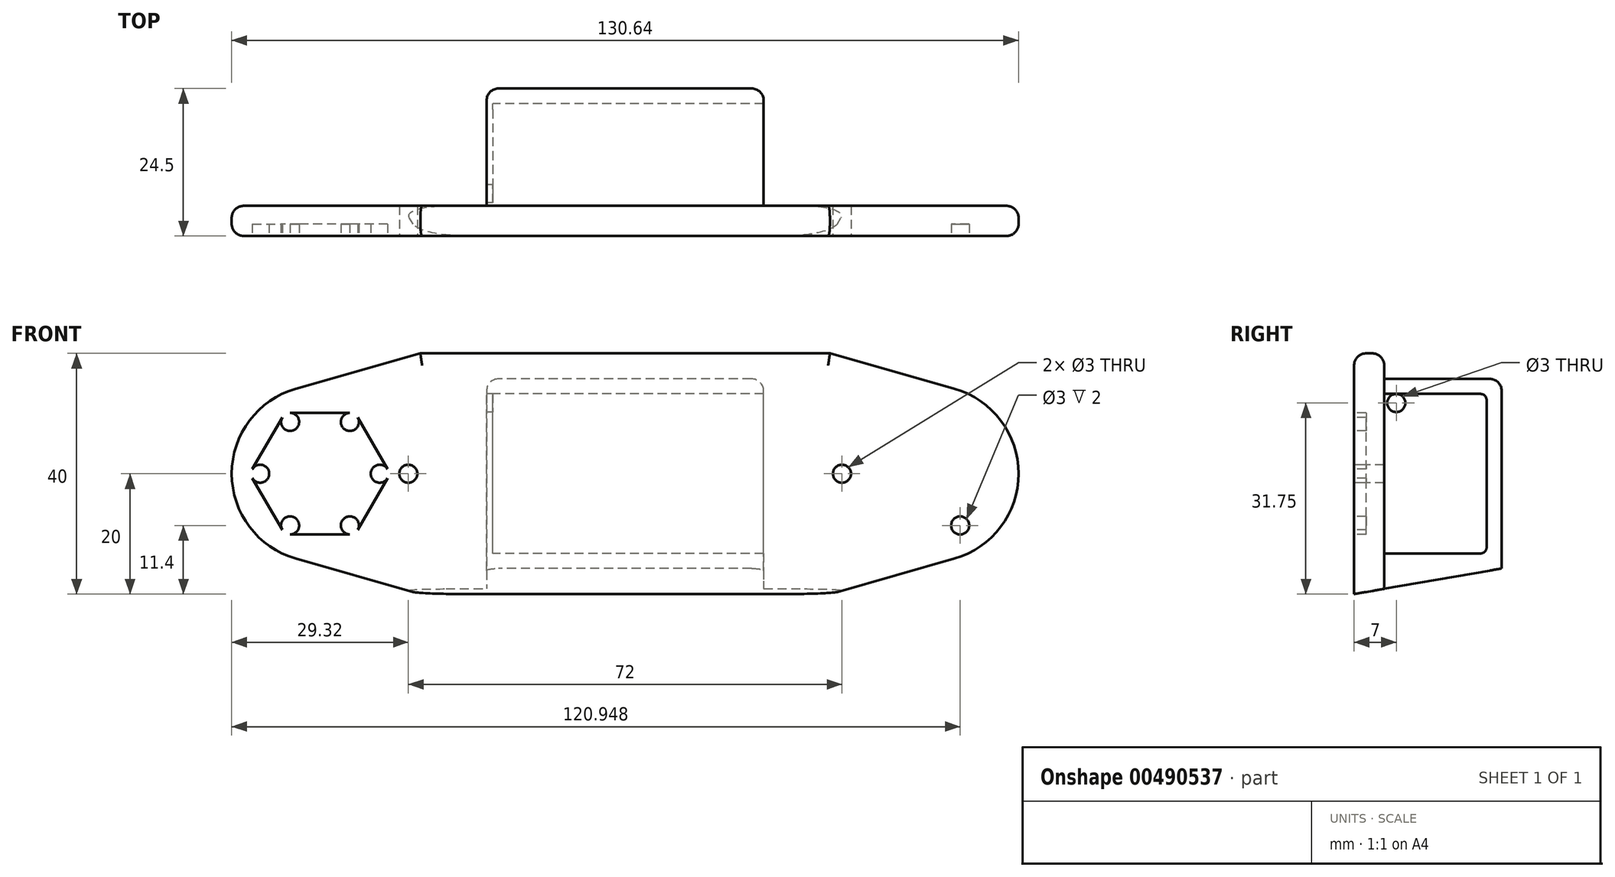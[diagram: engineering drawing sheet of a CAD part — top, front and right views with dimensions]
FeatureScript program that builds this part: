
annotation { "Feature Type Name" : "Feature", "Feature Type Description" : "" }
export const myFeature = defineFeature(function(context is Context, id is Id, definition is map)
    precondition{}
    {
        {
            var Q0;
            Q0=qCreatedBy(makeId("Front.planeOp"),FACE);
            var sketch = newSketch(context, id + "F0", { "sketchPlane" : qUnion([Q0])});
            skLineSegment(sketch, "E0.bottom", {"start": v(34, 30) * mm, "end": v(-34, 30) * mm});
            skLineSegment(sketch, "E0.top", {"start": v(34, -30) * mm, "end": v(-34, -30) * mm});
            skLineSegment(sketch, "E0.left", {"start": v(34, 30) * mm, "end": v(34, -30) * mm});
            skLineSegment(sketch, "E0.right", {"start": v(-34, 30) * mm, "end": v(-34, -30) * mm});
            skPoint(sketch, "E0.middle", {"position": v(0, 0) * mm});
            skSolve(sketch);
        }
        {
            var Q0;
            Q0=qCreatedBy(makeId("Front.planeOp"),FACE);
            var sketch = newSketch(context, id + "F1", { "sketchPlane" : qUnion([Q0])});
            skCircle(sketch, "E1.cCircle", {"center": v(-50.66, 0) * mm, "radius": 10.1 * mm, "construction": true});
            skLineSegment(sketch, "E1.0", {"start": v(-44.83, -10.1) * mm, "end": v(-56.5, -10.1) * mm});
            skLineSegment(sketch, "E1.1", {"start": v(-56.5, -10.1) * mm, "end": v(-62.32, 0) * mm});
            skLineSegment(sketch, "E1.2", {"start": v(-62.32, 0) * mm, "end": v(-56.5, 10.1) * mm});
            skLineSegment(sketch, "E1.3", {"start": v(-56.5, 10.1) * mm, "end": v(-44.83, 10.1) * mm});
            skLineSegment(sketch, "E1.4", {"start": v(-44.83, 10.1) * mm, "end": v(-39, 0) * mm});
            skLineSegment(sketch, "E1.5", {"start": v(-39, 0) * mm, "end": v(-44.83, -10.1) * mm});
            skPoint(sketch, "E1.0.midPoint", {"position": v(-50.66, -10.1) * mm});
            skCircle(sketch, "E2", {"center": v(-55.63, -8.6) * mm, "radius": 1.5 * mm});
            skCircle(sketch, "E3.1.0", {"center": v(-45.7, -8.6) * mm, "radius": 1.5 * mm});
            skCircle(sketch, "E3.2.0", {"center": v(-40.73, 0) * mm, "radius": 1.5 * mm});
            skCircle(sketch, "E3.3.0", {"center": v(-45.7, 8.6) * mm, "radius": 1.5 * mm});
            skCircle(sketch, "E3.4.0", {"center": v(-55.63, 8.6) * mm, "radius": 1.5 * mm});
            skCircle(sketch, "E3.5.0", {"center": v(-60.6, 0) * mm, "radius": 1.5 * mm});
            skCircle(sketch, "E4.MirrorC", {"center": v(55.63, -8.6) * mm, "radius": 1.5 * mm});
            skCircle(sketch, "E5.MirrorC", {"center": v(55.63, 8.6) * mm, "radius": 1.5 * mm});
            skCircle(sketch, "E6.MirrorC", {"center": v(45.7, -8.6) * mm, "radius": 1.5 * mm});
            skCircle(sketch, "E7.MirrorC", {"center": v(40.73, 0) * mm, "radius": 1.5 * mm});
            skCircle(sketch, "E8.MirrorC", {"center": v(50.66, 0) * mm, "radius": 10.1 * mm, "construction": true});
            skLineSegment(sketch, "E9.MirrorCS", {"start": v(44.83, -10.1) * mm, "end": v(56.5, -10.1) * mm});
            skLineSegment(sketch, "E10.MirrorCS", {"start": v(44.83, 10.1) * mm, "end": v(39, 0) * mm});
            skCircle(sketch, "E11.MirrorC", {"center": v(45.7, 8.6) * mm, "radius": 1.5 * mm});
            skLineSegment(sketch, "E12.MirrorCS", {"start": v(56.5, -10.1) * mm, "end": v(62.32, 0) * mm});
            skLineSegment(sketch, "E13.MirrorCS", {"start": v(39, 0) * mm, "end": v(44.83, -10.1) * mm});
            skPoint(sketch, "E14.MirrorP", {"position": v(50.66, -10.1) * mm});
            skLineSegment(sketch, "E15.MirrorCS", {"start": v(56.5, 10.1) * mm, "end": v(44.83, 10.1) * mm});
            skCircle(sketch, "E16.MirrorC", {"center": v(60.6, 0) * mm, "radius": 1.5 * mm});
            skLineSegment(sketch, "E17.MirrorCS", {"start": v(62.32, 0) * mm, "end": v(56.5, 10.1) * mm});
            skPoint(sketch, "E18", {"position": v(36, 0) * mm});
            skPoint(sketch, "E19.MirrorP", {"position": v(-36, 0) * mm});
            skSolve(sketch);
        }
        {
            var Q0;
            Q0=qCreatedBy(makeId("Front.planeOp"),FACE);
            var sketch = newSketch(context, id + "F2", { "sketchPlane" : qUnion([Q0])});
            skLineSegment(sketch, "E20.0.0", {"start": v(-34, -30) * mm, "end": v(34, -30) * mm, "construction": true});
            skLineSegment(sketch, "E20.0.1", {"start": v(34, -30) * mm, "end": v(34, 30) * mm, "construction": true});
            skLineSegment(sketch, "E20.0.2", {"start": v(34, 30) * mm, "end": v(-34, 30) * mm, "construction": true});
            skLineSegment(sketch, "E20.0.3", {"start": v(-34, 30) * mm, "end": v(-34, -30) * mm, "construction": true});
            skLineSegment(sketch, "E21.0.0", {"start": v(-39.43, 0.75) * mm, "end": v(-44.4, 9.35) * mm, "construction": true});
            skArc(sketch, "E21.0.1", {"start": v(-44.4, 9.35) * mm, "mid": v(-46.45, 7.3) * mm, "end": v(-45.7, 10.1) * mm, "construction": true});
            skLineSegment(sketch, "E21.0.2", {"start": v(-45.7, 10.1) * mm, "end": v(-55.63, 10.1) * mm, "construction": true});
            skArc(sketch, "E21.0.3", {"start": v(-55.63, 10.1) * mm, "mid": v(-54.88, 7.3) * mm, "end": v(-56.93, 9.35) * mm, "construction": true});
            skLineSegment(sketch, "E21.0.4", {"start": v(-56.93, 9.35) * mm, "end": v(-61.9, 0.75) * mm, "construction": true});
            skArc(sketch, "E21.0.5", {"start": v(-61.9, 0.75) * mm, "mid": v(-59.1, 0) * mm, "end": v(-61.9, -0.75) * mm, "construction": true});
            skLineSegment(sketch, "E21.0.6", {"start": v(-61.9, -0.75) * mm, "end": v(-56.93, -9.35) * mm, "construction": true});
            skArc(sketch, "E21.0.7", {"start": v(-56.93, -9.35) * mm, "mid": v(-54.88, -7.3) * mm, "end": v(-55.63, -10.1) * mm, "construction": true});
            skLineSegment(sketch, "E21.0.8", {"start": v(-55.63, -10.1) * mm, "end": v(-45.7, -10.1) * mm, "construction": true});
            skArc(sketch, "E21.0.9", {"start": v(-45.7, -10.1) * mm, "mid": v(-46.45, -7.3) * mm, "end": v(-44.4, -9.35) * mm, "construction": true});
            skLineSegment(sketch, "E21.0.10", {"start": v(-44.4, -9.35) * mm, "end": v(-39.43, -0.75) * mm, "construction": true});
            skArc(sketch, "E21.0.11", {"start": v(-39.43, -0.75) * mm, "mid": v(-42.23, 0) * mm, "end": v(-39.43, 0.75) * mm, "construction": true});
            skArc(sketch, "E22.0.0", {"start": v(45.7, 10.1) * mm, "mid": v(46.45, 7.3) * mm, "end": v(44.4, 9.35) * mm, "construction": true});
            skLineSegment(sketch, "E22.0.1", {"start": v(44.4, 9.35) * mm, "end": v(39.43, 0.75) * mm, "construction": true});
            skArc(sketch, "E22.0.2", {"start": v(39.43, 0.75) * mm, "mid": v(42.23, 0) * mm, "end": v(39.43, -0.75) * mm, "construction": true});
            skLineSegment(sketch, "E22.0.3", {"start": v(39.43, -0.75) * mm, "end": v(44.4, -9.35) * mm, "construction": true});
            skArc(sketch, "E22.0.4", {"start": v(44.4, -9.35) * mm, "mid": v(46.45, -7.3) * mm, "end": v(45.7, -10.1) * mm, "construction": true});
            skLineSegment(sketch, "E22.0.5", {"start": v(45.7, -10.1) * mm, "end": v(55.63, -10.1) * mm, "construction": true});
            skArc(sketch, "E22.0.6", {"start": v(55.63, -10.1) * mm, "mid": v(54.88, -7.3) * mm, "end": v(56.93, -9.35) * mm, "construction": true});
            skLineSegment(sketch, "E22.0.7", {"start": v(56.93, -9.35) * mm, "end": v(61.9, -0.75) * mm, "construction": true});
            skArc(sketch, "E22.0.8", {"start": v(61.9, -0.75) * mm, "mid": v(59.1, 0) * mm, "end": v(61.9, 0.75) * mm, "construction": true});
            skLineSegment(sketch, "E22.0.9", {"start": v(61.9, 0.75) * mm, "end": v(56.93, 9.35) * mm, "construction": true});
            skArc(sketch, "E22.0.10", {"start": v(56.93, 9.35) * mm, "mid": v(54.88, 7.3) * mm, "end": v(55.63, 10.1) * mm, "construction": true});
            skLineSegment(sketch, "E22.0.11", {"start": v(55.63, 10.1) * mm, "end": v(45.7, 10.1) * mm, "construction": true});
            skArc(sketch, "E23", {"start": v(-54.68, 14.1) * mm, "mid": v(-65.32, 0) * mm, "end": v(-54.68, -14.1) * mm});
            skPoint(sketch, "E23.centerSnap0", {"position": v(-50.66, 10.1) * mm});
            skPoint(sketch, "E24.0", {"position": v(50.66, 0) * mm});
            skArc(sketch, "E25", {"start": v(54.68, -14.1) * mm, "mid": v(65.32, 0) * mm, "end": v(54.68, 14.1) * mm});
            skLineSegment(sketch, "E26", {"start": v(-54.68, 14.1) * mm, "end": v(-34, 20) * mm});
            skLineSegment(sketch, "E27", {"start": v(-54.68, -14.1) * mm, "end": v(-34, -20) * mm});
            skLineSegment(sketch, "E28", {"start": v(-34, 20) * mm, "end": v(34, 20) * mm});
            skLineSegment(sketch, "E29", {"start": v(-34, -20) * mm, "end": v(34, -20) * mm});
            skLineSegment(sketch, "E30.MirrorCS", {"start": v(54.68, 14.1) * mm, "end": v(34, 20) * mm});
            skLineSegment(sketch, "E31.MirrorCS", {"start": v(54.68, -14.1) * mm, "end": v(34, -20) * mm});
            skSolve(sketch);
        }
        {
            var Q0;
            Q0=makeQuery(id+"F2.imprint","IMPRINT",FACE,{"disambiguationData":[TD([[makeQuery(id+"F2.imprint","IMPRINT",EDGE,{"derivedFrom":sQuery(id+"F2.wireOp",EDGE,"E23")}),1.0]])]});
            extrude(context, id + "F3", {"entities" : qUnion([Q0]), "oppositeDirection" : true, "depth" : 5 * mm});
        }
        {
            var Q0;
            {var subQ6=sQuery(id+"F1.wireOp",EDGE,"E1.0");var subQ13=sQuery(id+"F1.wireOp",EDGE,"E3.1.0");var subQ16=makeQuery(id+"F1.imprint","INTERSECT",VERTEX,{"derivedFrom":[subQ6,subQ13]});Q0=makeQuery(id+"F1.imprint","IMPRINT",FACE,{"disambiguationData":[TD([[makeQuery(id+"F1.imprint","IMPRINT",EDGE,{"disambiguationData":[TD([[subQ16,-1.0]])],"derivedFrom":subQ6}),-1.0]])]});}
            var Q1;
            {var subQ1=sQuery(id+"F1.wireOp",EDGE,"E4.MirrorC");var subQ15=sQuery(id+"F1.wireOp",EDGE,"E9.MirrorCS");var subQ16=makeQuery(id+"F1.imprint","INTERSECT",VERTEX,{"derivedFrom":[subQ1,subQ15]});Q1=makeQuery(id+"F1.imprint","IMPRINT",FACE,{"disambiguationData":[TD([[makeQuery(id+"F1.imprint","IMPRINT",EDGE,{"disambiguationData":[TD([[subQ16,-1.0]])],"derivedFrom":subQ1}),1.0]])]});}
            extrude(context, id + "F4", {"entities" : qUnion([Q0, Q1]), "operationType" : NewBodyOperationType.REMOVE, "oppositeDirection" : true, "depth" : 2 * mm});
        }
        {
            var Q0;
            Q0=qCreatedBy(makeId("Right.planeOp"),FACE);
            var sketch = newSketch(context, id + "F5", { "sketchPlane" : qUnion([Q0])});
            skLineSegment(sketch, "E32.0", {"start": v(5, -14.1) * mm, "end": v(5, 14.1) * mm, "construction": true});
            skLineSegment(sketch, "E33.bottom", {"start": v(22, -13.25) * mm, "end": v(5, -13.25) * mm});
            skLineSegment(sketch, "E33.top", {"start": v(22, 13.25) * mm, "end": v(5, 13.25) * mm});
            skLineSegment(sketch, "E33.left", {"start": v(22, -13.25) * mm, "end": v(22, 13.25) * mm});
            skLineSegment(sketch, "E33.right", {"start": v(5, -13.25) * mm, "end": v(5, 13.25) * mm});
            skPoint(sketch, "E33.middle", {"position": v(13.5, 0) * mm});
            skLineSegment(sketch, "E34.0", {"start": v(24.5, 15.75) * mm, "end": v(5, 15.75) * mm});
            skLineSegment(sketch, "E34.1", {"start": v(24.5, -15.75) * mm, "end": v(24.5, 15.75) * mm});
            skLineSegment(sketch, "E35", {"start": v(5, 13.25) * mm, "end": v(5, 15.75) * mm});
            skLineSegment(sketch, "E36", {"start": v(24.5, -15.75) * mm, "end": v(0, -20) * mm});
            skPoint(sketch, "E37.0", {"position": v(0, -20) * mm});
            skLineSegment(sketch, "E38", {"start": v(5, -13.25) * mm, "end": v(5, -19.13) * mm});
            skPoint(sketch, "E39.0", {"position": v(5, -20) * mm});
            skLineSegment(sketch, "E40", {"start": v(5, -19.13) * mm, "end": v(5, -20) * mm});
            skLineSegment(sketch, "E41", {"start": v(0, -20) * mm, "end": v(5, -20) * mm});
            skSolve(sketch);
        }
        {
            var Q0;
            Q0=makeQuery(id+"F5.imprint","IMPRINT",FACE,{"disambiguationData":[TD([[makeQuery(id+"F5.imprint","IMPRINT",EDGE,{"derivedFrom":sQuery(id+"F5.wireOp",EDGE,"E33.bottom")}),1.0]])]});
            extrude(context, id + "F6", {"entities" : qUnion([Q0]), "operationType" : NewBodyOperationType.ADD, "endBound" : BoundingType.SYMMETRIC, "depth" : 46 * mm});
        }
        {
            var Q0;
            Q0=makeQuery(id+"F5.imprint","IMPRINT",FACE,{"disambiguationData":[TD([[makeQuery(id+"F5.imprint","IMPRINT",EDGE,{"derivedFrom":sQuery(id+"F5.wireOp",EDGE,"E33.bottom")}),-1.0]])]});
            var Q1;
            Q1=makeQuery(id+"F6.opExtrude","CAP_FACE",FACE,{"disambiguationData":[OSD([sQuery(id+"F5.wireOp",EDGE,"E33.bottom"),sQuery(id+"F5.wireOp",EDGE,"E33.top"),sQuery(id+"F5.wireOp",EDGE,"E33.left"),sQuery(id+"F5.wireOp",EDGE,"E34.0"),sQuery(id+"F5.wireOp",EDGE,"E34.1"),sQuery(id+"F5.wireOp",EDGE,"E35"),sQuery(id+"F5.wireOp",EDGE,"E36"),sQuery(id+"F5.wireOp",EDGE,"oWYAaW46-Xd7K-HqAU-Cgo2-wgBWHUBuq2t6")])],"isStart":true});
            extrude(context, id + "F7", {"entities" : qUnion([Q0]), "operationType" : NewBodyOperationType.ADD, "endBound" : BoundingType.UP_TO_SURFACE, "oppositeDirection" : true, "endBoundEntityFace" : qUnion([Q1]), "depth" : 25 * mm, "hasSecondDirection" : true, "secondDirectionOppositeDirection" : true, "secondDirectionDepth" : 22 * mm});
        }
        {
            var Q0;
            Q0=sQuery(id+"F1.wireOp",VERTEX,"E19.MirrorP");
            var Q1;
            Q1=sQuery(id+"F1.wireOp",VERTEX,"E18");
            var Q2;
            Q2=makeQuery(id+"F3.opExtrude","SWEPT_BODY",BODY,{"disambiguationData":[OSD([sQuery(id+"F2.wireOp",EDGE,"E23"),sQuery(id+"F2.wireOp",EDGE,"E25"),sQuery(id+"F2.wireOp",EDGE,"E26"),sQuery(id+"F2.wireOp",EDGE,"E27"),sQuery(id+"F2.wireOp",EDGE,"E28"),sQuery(id+"F2.wireOp",EDGE,"E29"),sQuery(id+"F2.wireOp",EDGE,"E30.MirrorCS"),sQuery(id+"F2.wireOp",EDGE,"E31.MirrorCS")])]});
            hole(context, id + "F8", {"style" : HoleStyle.SIMPLE, "endStyle" : HoleEndStyle.THROUGH, "holeDiameter" : 3 * mm, "isTappedThrough" : true, "tappedDepth" : 12 * mm, "tapClearance" : 3, "locations" : qUnion([Q0, Q1]), "scope" : qUnion([Q2])});
        }
        {
            var Q0;
            {var subQ0=sQuery(id+"F5.wireOp",EDGE,"E38");var subQ1=sQuery(id+"F5.wireOp",EDGE,"E36");var subQ2=sQuery(id+"F5.wireOp",EDGE,"E35");var subQ3=sQuery(id+"F5.wireOp",EDGE,"E34.1");var subQ4=sQuery(id+"F5.wireOp",EDGE,"E34.0");var subQ5=sQuery(id+"F5.wireOp",EDGE,"E33.left");var subQ6=sQuery(id+"F5.wireOp",EDGE,"E33.top");var subQ7=sQuery(id+"F5.wireOp",EDGE,"E33.bottom");Q0=makeQuery(id+"F7.boolean.opBoolean","MERGE",FACE,{"derivedFrom":[makeQuery(id+"F6.opExtrude","CAP_FACE",FACE,{"disambiguationData":[OSD([subQ7,subQ6,subQ5,subQ4,subQ3,subQ2,subQ1,subQ0])],"isStart":true}),makeQuery(id+"F7.opExtrude","CAP_FACE",FACE,{"disambiguationData":[OSD([subQ7,subQ6,subQ5,subQ4,subQ3,subQ2,subQ1,subQ0])],"isStart":false})]});}
            var sketch = newSketch(context, id + "F9", { "sketchPlane" : qUnion([Q0])});
            skPoint(sketch, "E42", {"position": v(-7, 11.75) * mm});
            skSolve(sketch);
        }
        {
            var Q0;
            Q0=sQuery(id+"F9.wireOp",VERTEX,"E42");
            var Q1;
            Q1=makeQuery(id+"F3.opExtrude","SWEPT_BODY",BODY,{"disambiguationData":[OSD([sQuery(id+"F2.wireOp",EDGE,"E23"),sQuery(id+"F2.wireOp",EDGE,"E25"),sQuery(id+"F2.wireOp",EDGE,"E26"),sQuery(id+"F2.wireOp",EDGE,"E27"),sQuery(id+"F2.wireOp",EDGE,"E28"),sQuery(id+"F2.wireOp",EDGE,"E29"),sQuery(id+"F2.wireOp",EDGE,"E30.MirrorCS"),sQuery(id+"F2.wireOp",EDGE,"E31.MirrorCS")])]});
            hole(context, id + "F10", {"style" : HoleStyle.SIMPLE, "endStyle" : HoleEndStyle.THROUGH, "holeDiameter" : 3 * mm, "isTappedThrough" : true, "tappedDepth" : 12 * mm, "tapClearance" : 3, "locations" : qUnion([Q0]), "scope" : qUnion([Q1])});
        }
        {
            var Q0;
            {var subQ2=sQuery(id+"F5.wireOp",EDGE,"E40");Q0=makeQuery(id+"F5.imprint","IMPRINT",FACE,{"disambiguationData":[TD([[makeQuery(id+"F5.imprint","IMPRINT",EDGE,{"derivedFrom":subQ2}),-1.0]])]});}
            extrude(context, id + "F11", {"entities" : qUnion([Q0]), "operationType" : NewBodyOperationType.REMOVE, "endBound" : BoundingType.SYMMETRIC, "oppositeDirection" : true, "depth" : 100 * mm});
        }
        {
            var Q0;
            Q0=makeQuery(id+"F6.opExtrude","CAP_EDGE",EDGE,{"disambiguationData":[OSD([sQuery(id+"F5.wireOp",EDGE,"E34.0")])],"isStart":true});
            var Q1;
            Q1=makeQuery(id+"F6.opExtrude","CAP_EDGE",EDGE,{"disambiguationData":[OSD([sQuery(id+"F5.wireOp",EDGE,"E34.0")])],"isStart":false});
            var Q2;
            Q2=makeQuery(id+"F6.opExtrude","SWEPT_EDGE",EDGE,{"disambiguationData":[OSD([sQuery(id+"F5.wireOp",EDGE,"E34.0"),sQuery(id+"F5.wireOp",EDGE,"E35")])]});
            var Q3;
            {var subQ0=sQuery(id+"F5.wireOp",EDGE,"E38");var subQ1=sQuery(id+"F5.wireOp",EDGE,"E35");Q3=makeQuery(id+"F7.boolean.opBoolean","MERGE",EDGE,{"derivedFrom":[makeQuery(id+"F6.opExtrude","CAP_EDGE",EDGE,{"disambiguationData":[OSD([subQ1])],"isStart":true}),makeQuery(id+"F6.opExtrude","CAP_EDGE",EDGE,{"disambiguationData":[OSD([subQ0])],"isStart":true}),makeQuery(id+"F7.opExtrude","TWEAK_EDGE",EDGE,{"derivedFrom":[makeQuery(id+"F5.imprint","IMPRINT",EDGE,{"derivedFrom":sQuery(id+"F5.wireOp",EDGE,"E33.right")}),makeQuery(id+"F6.opExtrude","CAP_FACE",FACE,{"disambiguationData":[OSD([sQuery(id+"F5.wireOp",EDGE,"E33.bottom"),sQuery(id+"F5.wireOp",EDGE,"E33.top"),sQuery(id+"F5.wireOp",EDGE,"E33.left"),sQuery(id+"F5.wireOp",EDGE,"E34.0"),sQuery(id+"F5.wireOp",EDGE,"E34.1"),subQ1,sQuery(id+"F5.wireOp",EDGE,"E36"),subQ0])],"isStart":true})]})]});}
            var Q4;
            Q4=makeQuery(id+"F6.opExtrude","CAP_EDGE",EDGE,{"disambiguationData":[OSD([sQuery(id+"F5.wireOp",EDGE,"E38")])],"isStart":false});
            var Q5;
            Q5=makeQuery(id+"F6.opExtrude","CAP_EDGE",EDGE,{"disambiguationData":[OSD([sQuery(id+"F5.wireOp",EDGE,"E34.1")])],"isStart":false});
            var Q6;
            Q6=makeQuery(id+"F6.opExtrude","CAP_EDGE",EDGE,{"disambiguationData":[OSD([sQuery(id+"F5.wireOp",EDGE,"E34.1")])],"isStart":true});
            var Q7;
            Q7=makeQuery(id+"F6.opExtrude","SWEPT_EDGE",EDGE,{"disambiguationData":[OSD([sQuery(id+"F5.wireOp",EDGE,"E34.0"),sQuery(id+"F5.wireOp",EDGE,"E34.1")])]});
            var Q8;
            Q8=makeQuery(id+"F3.opExtrude","CAP_EDGE",EDGE,{"disambiguationData":[OSD([sQuery(id+"F2.wireOp",EDGE,"E25")])],"isStart":false});
            var Q9;
            Q9=makeQuery(id+"F3.opExtrude","CAP_EDGE",EDGE,{"disambiguationData":[OSD([sQuery(id+"F2.wireOp",EDGE,"E28")])],"isStart":false});
            var Q10;
            Q10=makeQuery(id+"F3.opExtrude","CAP_EDGE",EDGE,{"disambiguationData":[OSD([sQuery(id+"F2.wireOp",EDGE,"E26")])],"isStart":false});
            var Q11;
            Q11=makeQuery(id+"F3.opExtrude","CAP_EDGE",EDGE,{"disambiguationData":[OSD([sQuery(id+"F2.wireOp",EDGE,"E26")])],"isStart":true});
            var Q12;
            Q12=makeQuery(id+"F3.opExtrude","CAP_EDGE",EDGE,{"disambiguationData":[OSD([sQuery(id+"F2.wireOp",EDGE,"E28")])],"isStart":true});
            var Q13;
            Q13=makeQuery(id+"F3.opExtrude","CAP_EDGE",EDGE,{"disambiguationData":[OSD([sQuery(id+"F2.wireOp",EDGE,"E30.MirrorCS")])],"isStart":true});
            fillet(context, id + "F12", {"entities" : qUnion([Q0, Q1, Q2, Q3, Q4, Q5, Q6, Q7, Q8, Q9, Q10, Q11, Q12, Q13]), "radius" : 2 * mm, "tangentPropagation" : true, "allowEdgeOverflow" : false});
        }
        {
            var Q0;
            Q0=makeQuery(id+"F6.opExtrude","SWEPT_EDGE",EDGE,{"disambiguationData":[OSD([sQuery(id+"F5.wireOp",EDGE,"E33.top"),sQuery(id+"F5.wireOp",EDGE,"E33.right"),sQuery(id+"F5.wireOp",EDGE,"E35")])]});
            var Q1;
            Q1=makeQuery(id+"F7.opExtrude","CAP_EDGE",EDGE,{"disambiguationData":[OSD([sQuery(id+"F5.wireOp",EDGE,"E33.right")])],"isStart":true});
            var Q2;
            Q2=makeQuery(id+"F6.opExtrude","SWEPT_EDGE",EDGE,{"disambiguationData":[OSD([sQuery(id+"F5.wireOp",EDGE,"E33.bottom"),sQuery(id+"F5.wireOp",EDGE,"E33.right"),sQuery(id+"F5.wireOp",EDGE,"E38")])]});
            var Q3;
            Q3=makeQuery(id+"F6.opExtrude","SWEPT_EDGE",EDGE,{"disambiguationData":[OSD([sQuery(id+"F5.wireOp",EDGE,"E33.bottom"),sQuery(id+"F5.wireOp",EDGE,"E33.left")])]});
            var Q4;
            Q4=makeQuery(id+"F6.opExtrude","SWEPT_EDGE",EDGE,{"disambiguationData":[OSD([sQuery(id+"F5.wireOp",EDGE,"E33.top"),sQuery(id+"F5.wireOp",EDGE,"E33.left")])]});
            fillet(context, id + "F13", {"entities" : qUnion([Q0, Q1, Q2, Q3, Q4]), "radius" : 1 * mm, "tangentPropagation" : true, "allowEdgeOverflow" : false});
        }
    });
